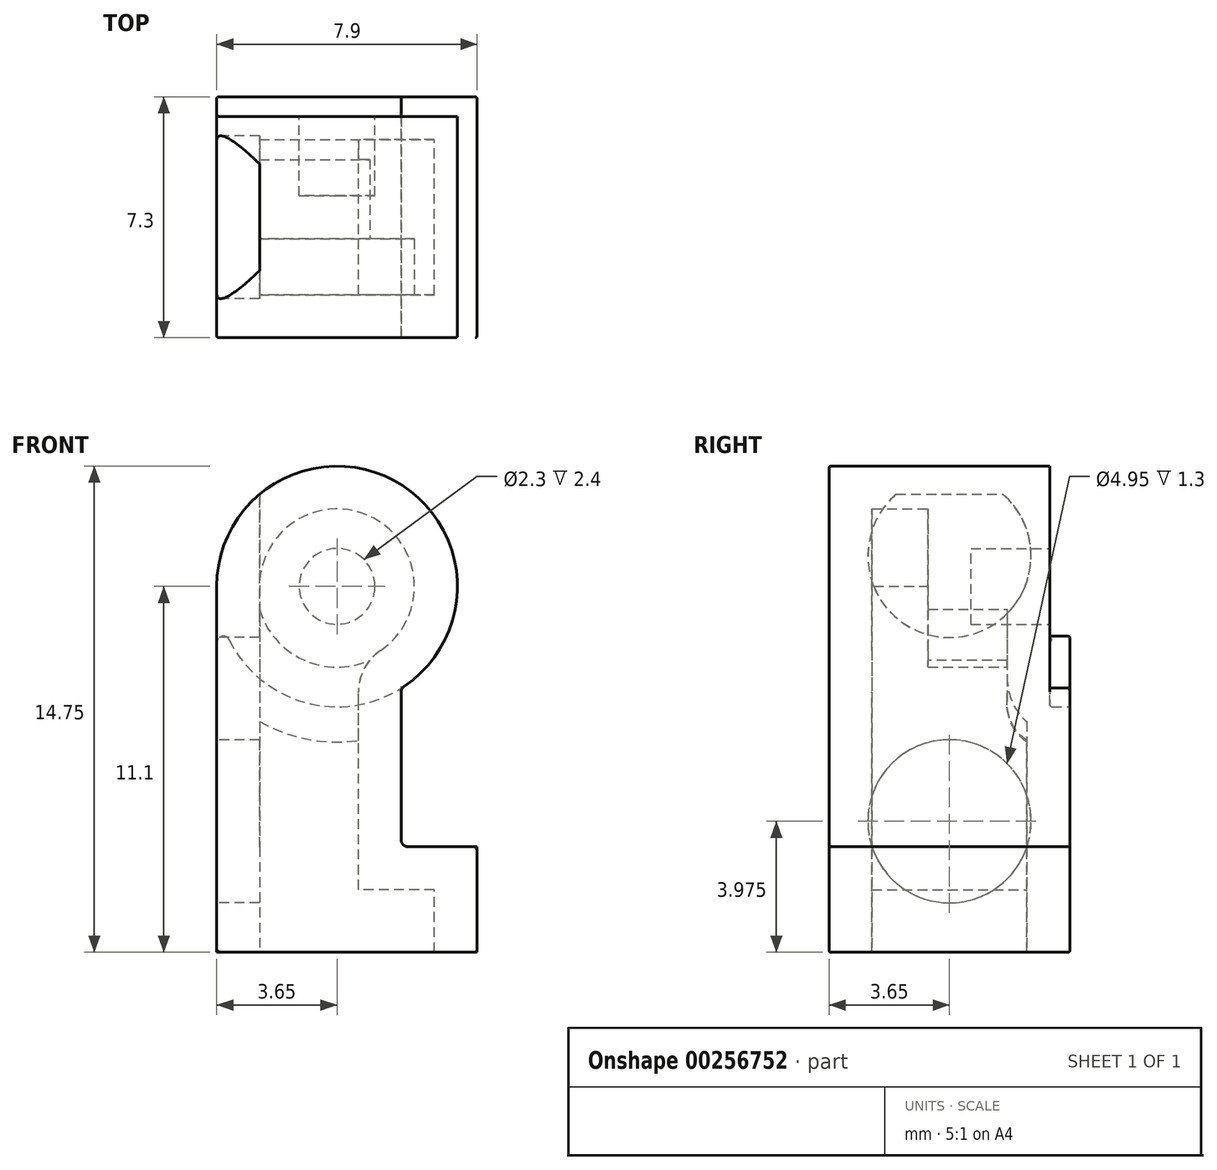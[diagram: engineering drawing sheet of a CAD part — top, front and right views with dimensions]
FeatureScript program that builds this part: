
annotation { "Feature Type Name" : "Feature", "Feature Type Description" : "" }
export const myFeature = defineFeature(function(context is Context, id is Id, definition is map)
    precondition{}
    {
        {
            var Q0;
            Q0=qCreatedBy(makeId("Front.planeOp"),FACE);
            var sketch = newSketch(context, id + "F0", { "sketchPlane" : qUnion([Q0])});
            skArc(sketch, "E0", {"start": v(1.95, -3.09) * mm, "mid": v(1.76, 3.2) * mm, "end": v(-3.65, 0) * mm});
            skLineSegment(sketch, "E1", {"start": v(-3.65, 0) * mm, "end": v(-3.65, -11.1) * mm});
            skLineSegment(sketch, "E2", {"start": v(-3.65, -11.1) * mm, "end": v(4.25, -11.1) * mm});
            skLineSegment(sketch, "E3", {"start": v(4.25, -11.1) * mm, "end": v(4.25, -7.9) * mm});
            skLineSegment(sketch, "E4", {"start": v(4.25, -7.9) * mm, "end": v(1.95, -7.9) * mm});
            skLineSegment(sketch, "E5", {"start": v(1.95, -7.9) * mm, "end": v(1.95, -3.09) * mm});
            skSolve(sketch);
        }
        {
            var Q0;
            Q0=makeQuery(id+"F0.imprint","IMPRINT",FACE,{"disambiguationData":[TD([[makeQuery(id+"F0.imprint","IMPRINT",EDGE,{"derivedFrom":sQuery(id+"F0.wireOp",EDGE,"E0")}),1.0]])]});
            extrude(context, id + "F1", {"entities" : qUnion([Q0]), "depth" : 7.3 * mm});
        }
        {
            var Q0;
            Q0=qCreatedBy(makeId("Front.planeOp"),FACE);
            var sketch = newSketch(context, id + "F2", { "sketchPlane" : qUnion([Q0])});
            skCircle(sketch, "E6", {"center": v(0, 0) * mm, "radius": 3.65 * mm});
            skSolve(sketch);
        }
        {
            var Q0;
            Q0=makeQuery(id+"F2.imprint","IMPRINT",FACE,{"disambiguationData":[TD([[makeQuery(id+"F2.imprint","IMPRINT",EDGE,{"derivedFrom":sQuery(id+"F2.wireOp",EDGE,"E6")}),1.0]])]});
            extrude(context, id + "F3", {"entities" : qUnion([Q0]), "operationType" : NewBodyOperationType.REMOVE, "depth" : 0.6 * mm});
        }
        {
            var Q0;
            Q0=qCreatedBy(makeId("Front.planeOp"),FACE);
            var sketch = newSketch(context, id + "F4", { "sketchPlane" : qUnion([Q0])});
            skCircle(sketch, "E7", {"center": v(0, 0) * mm, "radius": 1.15 * mm});
            skSolve(sketch);
        }
        {
            var Q0;
            Q0=makeQuery(id+"F4.imprint","IMPRINT",FACE,{"disambiguationData":[TD([[makeQuery(id+"F4.imprint","IMPRINT",EDGE,{"derivedFrom":sQuery(id+"F4.wireOp",EDGE,"E7")}),1.0]])]});
            extrude(context, id + "F5", {"entities" : qUnion([Q0]), "operationType" : NewBodyOperationType.REMOVE, "depth" : 3 * mm});
        }
        {
            var Q0;
            {var subQ0=sQuery(id+"F0.wireOp",EDGE,"E5");Q0=makeQuery(id+"F3.boolean.opBoolean","SPLIT",EDGE,{"disambiguationData":[topologyDisambiguationEdgeConnected([makeQuery(id+"F3.opExtrude","SWEPT_FACE",FACE,{"disambiguationData":[OSD([sQuery(id+"F2.wireOp",EDGE,"E6")])]})])],"derivedFrom":makeQuery(id+"F1.opExtrude","SWEPT_EDGE",EDGE,{"disambiguationData":[OSD([sQuery(id+"F0.wireOp",EDGE,"E0"),subQ0])]})});}
            var Q1;
            {var subQ0=sQuery(id+"F0.wireOp",EDGE,"E1");Q1=makeQuery(id+"F3.boolean.opBoolean","SPLIT",EDGE,{"disambiguationData":[topologyDisambiguationEdgeConnected([makeQuery(id+"F3.opExtrude","SWEPT_FACE",FACE,{"disambiguationData":[OSD([sQuery(id+"F2.wireOp",EDGE,"E6")])]})])],"derivedFrom":makeQuery(id+"F1.opExtrude","SWEPT_EDGE",EDGE,{"disambiguationData":[OSD([sQuery(id+"F0.wireOp",EDGE,"E0"),subQ0])]})});}
            fillet(context, id + "F6", {"entities" : qUnion([Q0, Q1]), "radius" : 0.2 * mm, "tangentPropagation" : true, "allowEdgeOverflow" : false});
        }
        {
            var Q0;
            {var subQ0=sQuery(id+"F2.wireOp",EDGE,"E6");Q0=makeQuery(id+"F3.boolean.opBoolean","COPY",EDGE,{"disambiguationData":[topologyDisambiguationEdgeConnected([makeQuery(id+"F3.opExtrude","SWEPT_FACE",FACE,{"disambiguationData":[OSD([subQ0])]})])],"derivedFrom":makeQuery(id+"F3.opExtrude","CAP_EDGE",EDGE,{"disambiguationData":[OSD([subQ0])],"isStart":false})});}
            fillet(context, id + "F7", {"entities" : qUnion([Q0]), "radius" : 0.05 * mm, "tangentPropagation" : true, "allowEdgeOverflow" : false});
        }
        {
            var Q0;
            Q0=makeQuery(id+"F1.opExtrude","SWEPT_FACE",FACE,{"disambiguationData":[OSD([sQuery(id+"F0.wireOp",EDGE,"E2")])]});
            shell(context, id + "F8", {"entities" : qUnion([Q0]), "thickness" : 1.3 * mm});
        }
        {
            var Q0;
            Q0=makeQuery(id+"F1.opExtrude","SWEPT_FACE",FACE,{"disambiguationData":[OSD([sQuery(id+"F0.wireOp",EDGE,"E1")])]});
            var sketch = newSketch(context, id + "F9", { "sketchPlane" : qUnion([Q0])});
            skCircle(sketch, "E8", {"center": v(3.65, -7.12) * mm, "radius": 2.48 * mm});
            skLineSegment(sketch, "E9", {"start": v(3.65, -11.1) * mm, "end": v(3.65, -6.01) * mm, "construction": true});
            skCircle(sketch, "E10", {"center": v(3.65, 0.92) * mm, "radius": 2.48 * mm});
            skSolve(sketch);
        }
        {
            var Q0;
            Q0 = qSketchRegion(id + "F9", true);
            var Q1;
            Q1=makeQuery(id+"F8.opShell","OFFSET_FACE",FACE,{"disambiguationData":[OSD([sQuery(id+"F0.wireOp",EDGE,"E1")])]});
            extrude(context, id + "F10", {"entities" : qUnion([Q0]), "operationType" : NewBodyOperationType.REMOVE, "endBound" : BoundingType.UP_TO_SURFACE, "oppositeDirection" : true, "endBoundEntityFace" : qUnion([Q1]), "depth" : 25 * mm});
        }
        {
            var Q0;
            {var subQ0=sQuery(id+"F0.wireOp",EDGE,"E0");var subQ1=sQuery(id+"F0.wireOp",EDGE,"E5");Q0=makeQuery(id+"F3.boolean.opBoolean","SPLIT",EDGE,{"disambiguationData":[topologyDisambiguationEdgeConnected([makeQuery(id+"F1.opExtrude","SWEPT_FACE",FACE,{"disambiguationData":[OSD([subQ0])]})])],"derivedFrom":makeQuery(id+"F1.opExtrude","SWEPT_EDGE",EDGE,{"disambiguationData":[OSD([subQ0,subQ1])]})});}
            var Q1;
            Q1=makeQuery(id+"F1.opExtrude","SWEPT_EDGE",EDGE,{"disambiguationData":[OSD([sQuery(id+"F0.wireOp",EDGE,"E4"),sQuery(id+"F0.wireOp",EDGE,"E5")])]});
            fillet(context, id + "F11", {"entities" : qUnion([Q0, Q1]), "radius" : 0.2 * mm, "tangentPropagation" : true, "allowEdgeOverflow" : false});
        }
        {
            var Q0;
            Q0=makeQuery(id+"F1.opExtrude","CAP_FACE",FACE,{"disambiguationData":[OSD([sQuery(id+"F0.wireOp",EDGE,"E0"),sQuery(id+"F0.wireOp",EDGE,"E1"),sQuery(id+"F0.wireOp",EDGE,"E2"),sQuery(id+"F0.wireOp",EDGE,"E3"),sQuery(id+"F0.wireOp",EDGE,"E4"),sQuery(id+"F0.wireOp",EDGE,"E5")])],"isStart":false});
            var Q1;
            Q1=makeQuery(id+"F1.opExtrude","CAP_FACE",FACE,{"disambiguationData":[OSD([sQuery(id+"F0.wireOp",EDGE,"E0"),sQuery(id+"F0.wireOp",EDGE,"E1"),sQuery(id+"F0.wireOp",EDGE,"E2"),sQuery(id+"F0.wireOp",EDGE,"E3"),sQuery(id+"F0.wireOp",EDGE,"E4"),sQuery(id+"F0.wireOp",EDGE,"E5")])],"isStart":true});
            fillet(context, id + "F12", {"entities" : qUnion([Q0, Q1]), "radius" : 0.05 * mm, "tangentPropagation" : true, "allowEdgeOverflow" : false});
        }
    });
